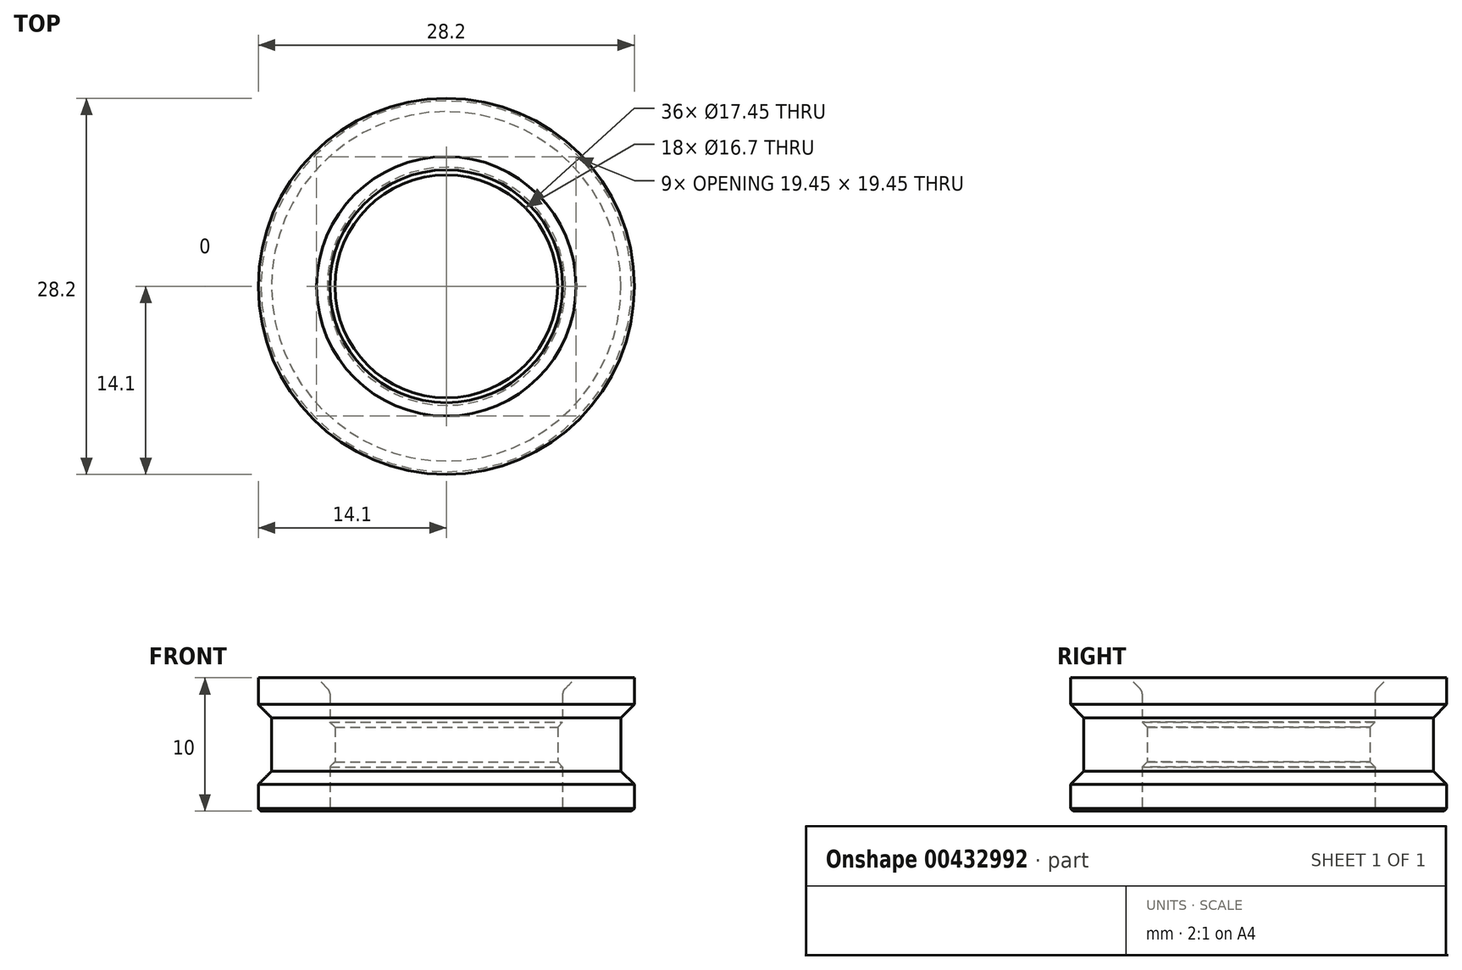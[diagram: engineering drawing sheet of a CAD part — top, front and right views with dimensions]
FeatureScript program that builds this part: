
annotation { "Feature Type Name" : "Feature", "Feature Type Description" : "" }
export const myFeature = defineFeature(function(context is Context, id is Id, definition is map)
    precondition{}
    {
        {
            var Q0;
            Q0=qCreatedBy(makeId("Front.planeOp"),FACE);
            var sketch = newSketch(context, id + "F0", { "sketchPlane" : qUnion([Q0])});
            skLineSegment(sketch, "E0", {"start": v(-8.35, 0) * mm, "end": v(-8.35, 1.3) * mm});
            skLineSegment(sketch, "E1", {"start": v(-8.35, 1.3) * mm, "end": v(-8.73, 1.67) * mm});
            skLineSegment(sketch, "E2", {"start": v(-8.73, 1.67) * mm, "end": v(-8.73, 5) * mm});
            skLineSegment(sketch, "E3", {"start": v(-8.72, 5) * mm, "end": v(-14.1, 5) * mm});
            skLineSegment(sketch, "E4", {"start": v(-14.1, 5) * mm, "end": v(-14.1, 3) * mm});
            skLineSegment(sketch, "E5", {"start": v(-14.1, 3) * mm, "end": v(-13.1, 2) * mm});
            skLineSegment(sketch, "E6", {"start": v(-13.1, 2) * mm, "end": v(-13.1, 0) * mm});
            skLineSegment(sketch, "E7.MirrorCS", {"start": v(-13.1, -2) * mm, "end": v(-13.1, 0) * mm});
            skLineSegment(sketch, "E8.MirrorCS", {"start": v(-14.1, -3) * mm, "end": v(-13.1, -2) * mm});
            skLineSegment(sketch, "E9.MirrorCS", {"start": v(-14.1, -5) * mm, "end": v(-14.1, -3) * mm});
            skLineSegment(sketch, "E10.MirrorCS", {"start": v(-8.72, -5) * mm, "end": v(-14.1, -5) * mm});
            skLineSegment(sketch, "E11.MirrorCS", {"start": v(-8.72, -1.67) * mm, "end": v(-8.72, -5) * mm});
            skLineSegment(sketch, "E12.MirrorCS", {"start": v(-8.35, -1.3) * mm, "end": v(-8.73, -1.67) * mm});
            skLineSegment(sketch, "E13.MirrorCS", {"start": v(-8.35, 0) * mm, "end": v(-8.35, -1.3) * mm});
            skLineSegment(sketch, "E14", {"start": v(0, 0) * mm, "end": v(0, 15.53) * mm});
            skSolve(sketch);
        }
        {
            var Q0;
            Q0=makeQuery(id+"F0.imprint","IMPRINT",FACE,{"disambiguationData":[TD([[makeQuery(id+"F0.imprint","IMPRINT",EDGE,{"derivedFrom":sQuery(id+"F0.wireOp",EDGE,"E0")}),1.0]])]});
            var Q1;
            Q1=sQuery(id+"F0.wireOp",EDGE,"E14");
            revolve(context, id + "F1", {"entities" : qUnion([Q0]), "axis" : qUnion([Q1]), "revolveType" : RevolveType.FULL});
        }
        {
            var Q0;
            Q0=makeQuery(id+"F1.opRevolve","SWEPT_EDGE",EDGE,{"disambiguationData":[OSD([sQuery(id+"F0.wireOp",EDGE,"E2"),sQuery(id+"F0.wireOp",EDGE,"E3")])]});
            chamfer(context, id + "F2", {"entities" : qUnion([Q0]), "width" : 1 * mm});
        }
        {
            var Q0;
            {var subQ0=sQuery(id+"F0.wireOp",EDGE,"E2");Q0=makeQuery(id+"F2.opChamfer","BLEND_EDGE",EDGE,{"blendedFrom":[makeQuery(id+"F1.opRevolve","SWEPT_EDGE",EDGE,{"disambiguationData":[OSD([subQ0,sQuery(id+"F0.wireOp",EDGE,"E3")])]}),makeQuery(id+"F1.opRevolve","SWEPT_FACE",FACE,{"disambiguationData":[OSD([subQ0])]})],"blendedInto":[makeQuery(id+"F1.opRevolve","SWEPT_FACE",FACE,{"disambiguationData":[OSD([subQ0])]})]});}
            fillet(context, id + "F3", {"entities" : qUnion([Q0]), "radius" : 0.5 * mm, "allowEdgeOverflow" : false});
        }
        {
            var Q0;
            Q0=makeQuery(id+"F1.opRevolve","SWEPT_FACE",FACE,{"disambiguationData":[OSD([sQuery(id+"F0.wireOp",EDGE,"E10.MirrorCS")])]});
            chamfer(context, id + "F4", {"entities" : qUnion([Q0]), "width" : 0.2 * mm});
        }
    });
